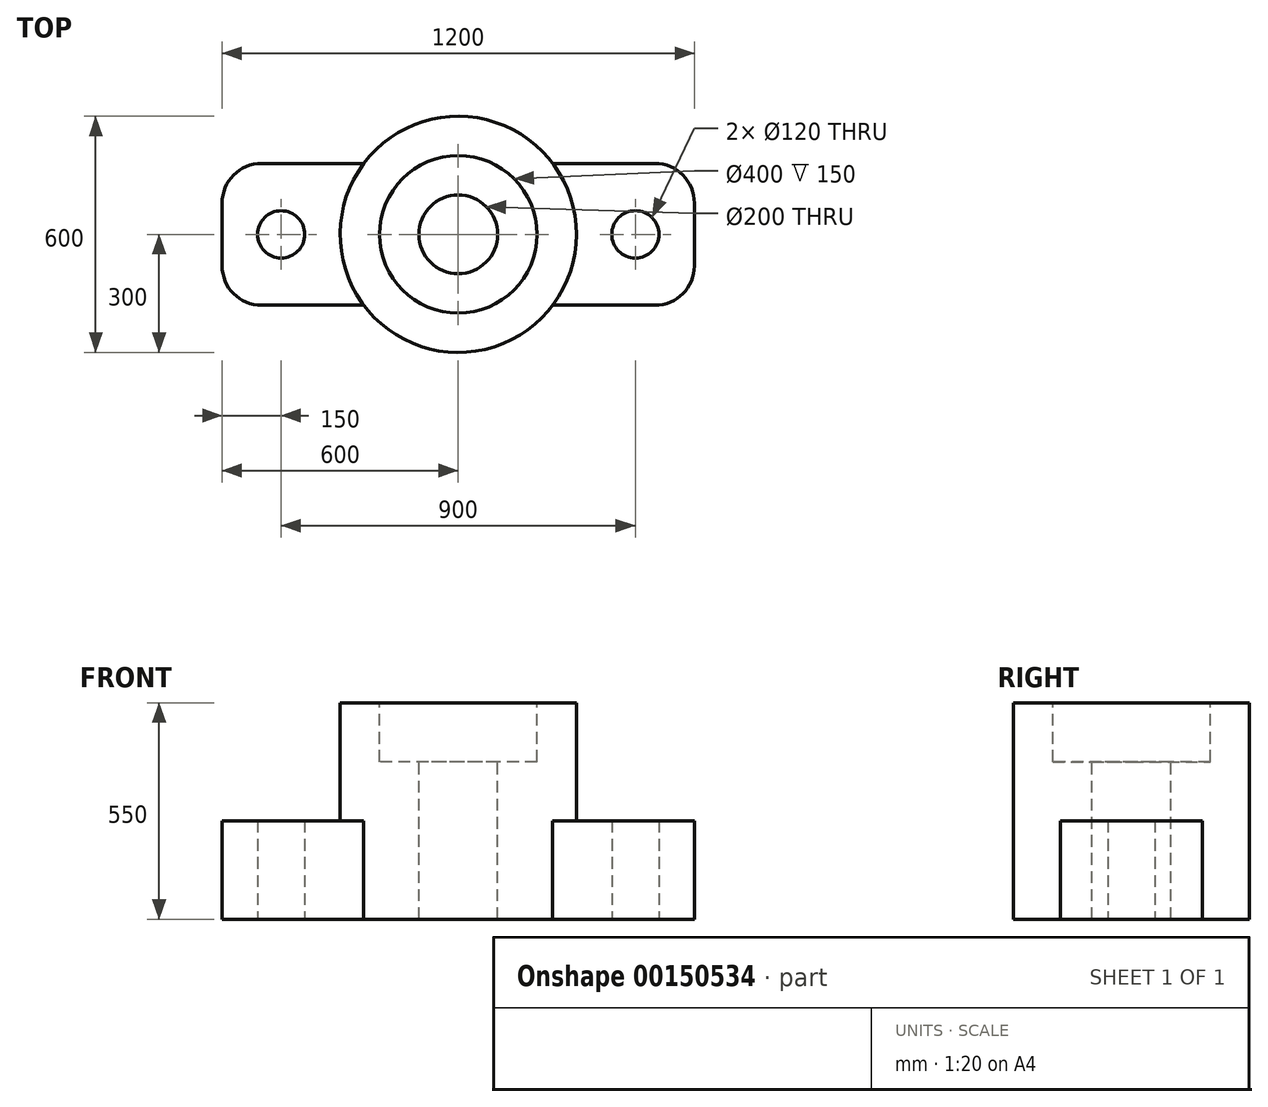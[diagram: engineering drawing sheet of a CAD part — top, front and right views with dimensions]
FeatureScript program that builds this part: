
annotation { "Feature Type Name" : "Feature", "Feature Type Description" : "" }
export const myFeature = defineFeature(function(context is Context, id is Id, definition is map)
    precondition{}
    {
        {
            var Q0;
            Q0=qCreatedBy(makeId("Top.planeOp"),FACE);
            var sketch = newSketch(context, id + "F0", { "sketchPlane" : qUnion([Q0])});
            skCircle(sketch, "E0", {"center": v(0, 0) * mm, "radius": 300 * mm});
            skSolve(sketch);
        }
        {
            var Q0;
            Q0=makeQuery(id+"F0.imprint","IMPRINT",FACE,{"disambiguationData":[TD([[makeQuery(id+"F0.imprint","IMPRINT",EDGE,{"derivedFrom":sQuery(id+"F0.wireOp",EDGE,"E0")}),1.0]])]});
            extrude(context, id + "F1", {"entities" : qUnion([Q0]), "depth" : 550 * mm});
        }
        {
            var Q0;
            Q0=makeQuery(id+"F1.opExtrude","CAP_FACE",FACE,{"disambiguationData":[OSD([sQuery(id+"F0.wireOp",EDGE,"E0")])],"isStart":false});
            var sketch = newSketch(context, id + "F2", { "sketchPlane" : qUnion([Q0])});
            skCircle(sketch, "E1", {"center": v(0, 0) * mm, "radius": 200 * mm});
            skSolve(sketch);
        }
        {
            var Q0;
            Q0 = qSketchRegion(id + "F2", true);
            extrude(context, id + "F3", {"entities" : qUnion([Q0]), "operationType" : NewBodyOperationType.REMOVE, "oppositeDirection" : true, "depth" : 150 * mm});
        }
        {
            var Q0;
            Q0=makeQuery(id+"F3.boolean.opBoolean","COPY",FACE,{"derivedFrom":makeQuery(id+"F3.opExtrude","CAP_FACE",FACE,{"disambiguationData":[OSD([sQuery(id+"F2.wireOp",EDGE,"E1")])],"isStart":false})});
            var sketch = newSketch(context, id + "F4", { "sketchPlane" : qUnion([Q0])});
            skCircle(sketch, "E2", {"center": v(0, 0) * mm, "radius": 100 * mm});
            skSolve(sketch);
        }
        {
            var Q0;
            Q0=makeQuery(id+"F1.opExtrude","CAP_FACE",FACE,{"disambiguationData":[OSD([sQuery(id+"F0.wireOp",EDGE,"E0")])],"isStart":true});
            var sketch = newSketch(context, id + "F5", { "sketchPlane" : qUnion([Q0])});
            skLineSegment(sketch, "E3.bottom", {"start": v(500, 180) * mm, "end": v(-500, 180) * mm});
            skLineSegment(sketch, "E3.top", {"start": v(500, -180) * mm, "end": v(-500, -180) * mm});
            skLineSegment(sketch, "E3.left", {"start": v(600, 80) * mm, "end": v(600, -80) * mm});
            skLineSegment(sketch, "E3.right", {"start": v(-600, 80) * mm, "end": v(-600, -80) * mm});
            skPoint(sketch, "E3.middle", {"position": v(0, 0) * mm});
            skPoint(sketch, "E4.visualSharp", {"position": v(-600, 180) * mm});
            skArc(sketch, "E4.filletArc", {"start": v(-500, 180) * mm, "mid": v(-570.71, 150.71) * mm, "end": v(-600, 80) * mm});
            skPoint(sketch, "E5.visualSharp", {"position": v(-600, -180) * mm});
            skArc(sketch, "E5.filletArc", {"start": v(-600, -80) * mm, "mid": v(-570.71, -150.71) * mm, "end": v(-500, -180) * mm});
            skPoint(sketch, "E6.visualSharp", {"position": v(600, -180) * mm});
            skArc(sketch, "E6.filletArc", {"start": v(500, -180) * mm, "mid": v(570.71, -150.71) * mm, "end": v(600, -80) * mm});
            skPoint(sketch, "E7.visualSharp", {"position": v(600, 180) * mm});
            skArc(sketch, "E7.filletArc", {"start": v(600, 80) * mm, "mid": v(570.71, 150.71) * mm, "end": v(500, 180) * mm});
            skCircle(sketch, "E8", {"center": v(-450, 0) * mm, "radius": 60 * mm});
            skCircle(sketch, "E9", {"center": v(450, 0) * mm, "radius": 60 * mm});
            skSolve(sketch);
        }
        {
            var Q0;
            Q0 = qSketchRegion(id + "F5", true);
            extrude(context, id + "F6", {"entities" : qUnion([Q0]), "operationType" : NewBodyOperationType.ADD, "oppositeDirection" : true, "depth" : 250 * mm});
        }
        {
            var Q0;
            Q0=makeQuery(id+"F4.imprint","IMPRINT",FACE,{"disambiguationData":[TD([[makeQuery(id+"F4.imprint","IMPRINT",EDGE,{"derivedFrom":sQuery(id+"F4.wireOp",EDGE,"E2")}),1.0]])]});
            extrude(context, id + "F7", {"entities" : qUnion([Q0]), "operationType" : NewBodyOperationType.REMOVE, "endBound" : BoundingType.THROUGH_ALL, "oppositeDirection" : true, "depth" : 25 * mm});
        }
    });
